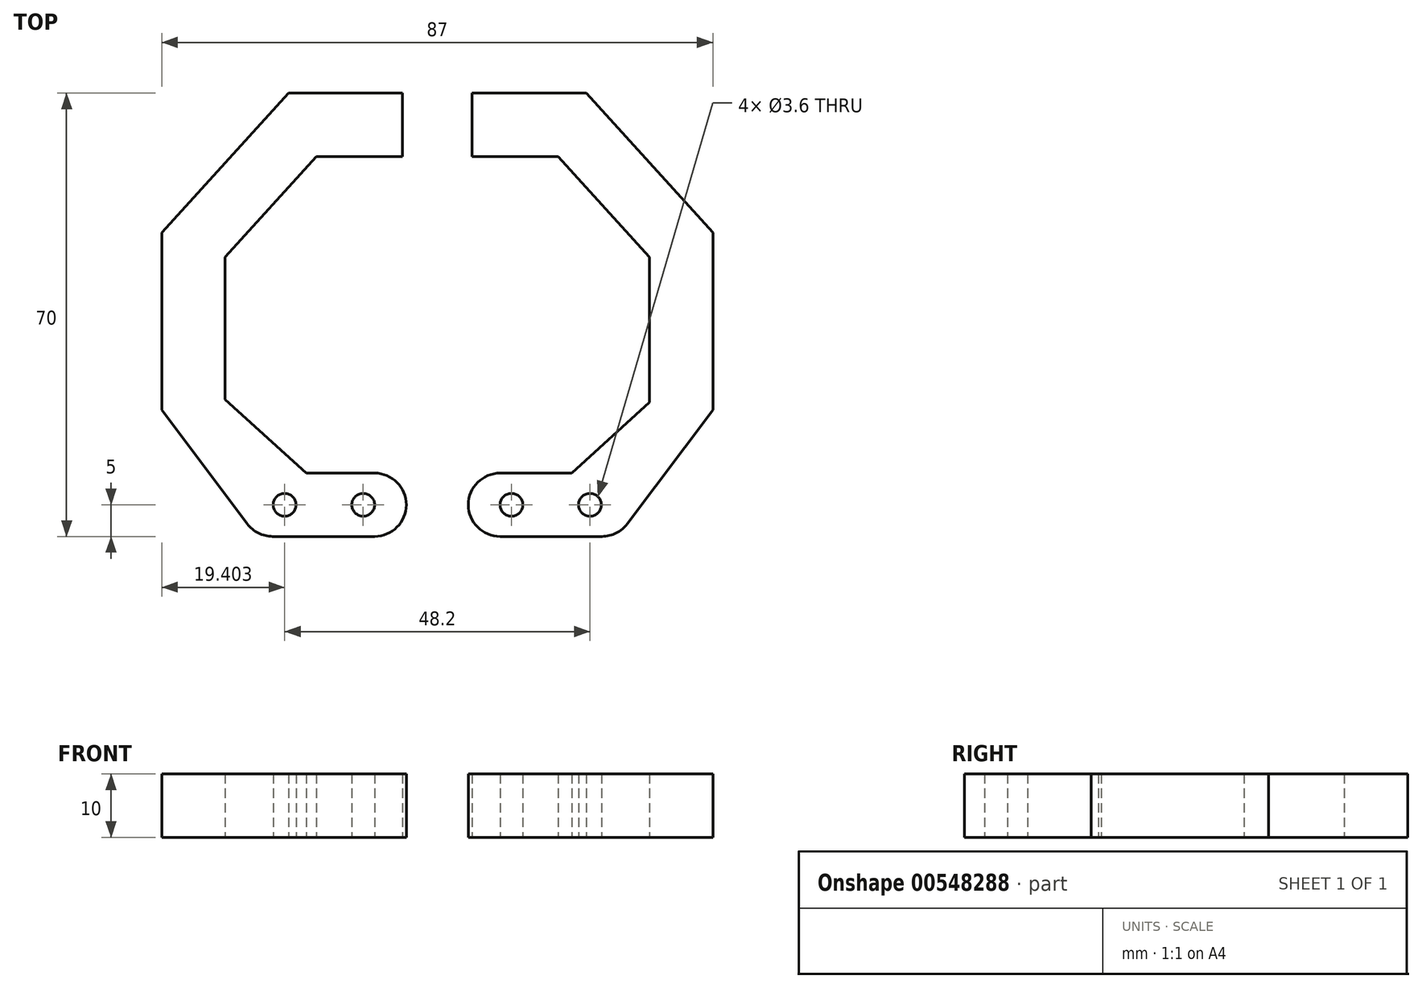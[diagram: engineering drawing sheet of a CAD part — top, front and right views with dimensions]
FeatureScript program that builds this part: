
annotation { "Feature Type Name" : "Feature", "Feature Type Description" : "" }
export const myFeature = defineFeature(function(context is Context, id is Id, definition is map)
    precondition{}
    {
        {
            var Q0;
            Q0=qCreatedBy(makeId("Top.planeOp"),FACE);
            var sketch = newSketch(context, id + "F0", { "sketchPlane" : qUnion([Q0])});
            skLineSegment(sketch, "E0.bottom", {"start": v(28.48, -32.9) * mm, "end": v(4.88, -32.9) * mm});
            skLineSegment(sketch, "E0.top", {"start": v(23.48, 37.1) * mm, "end": v(5.48, 37.1) * mm});
            skLineSegment(sketch, "E0.left", {"start": v(43.48, -12.9) * mm, "end": v(43.48, 15.1) * mm});
            skLineSegment(sketch, "E0.right", {"start": v(-43.52, -12.9) * mm, "end": v(-43.52, 15.1) * mm});
            skPoint(sketch, "E0.middle", {"position": v(-0.02, 2.1) * mm});
            skLineSegment(sketch, "E1", {"start": v(-43.52, -12.9) * mm, "end": v(-28.52, -32.9) * mm});
            skLineSegment(sketch, "E2", {"start": v(28.48, -32.9) * mm, "end": v(43.48, -12.9) * mm});
            skLineSegment(sketch, "E3", {"start": v(-43.52, 15.1) * mm, "end": v(-23.52, 37.1) * mm});
            skLineSegment(sketch, "E4", {"start": v(43.48, 15.1) * mm, "end": v(23.48, 37.1) * mm});
            skLineSegment(sketch, "E5", {"start": v(-23.52, 37.1) * mm, "end": v(-5.52, 37.1) * mm});
            skLineSegment(sketch, "E6", {"start": v(-5.52, 37.1) * mm, "end": v(-5.52, 27.1) * mm});
            skLineSegment(sketch, "E7", {"start": v(-5.52, 27.1) * mm, "end": v(-19.1, 27.1) * mm});
            skLineSegment(sketch, "E8", {"start": v(-19.1, 27.1) * mm, "end": v(-33.52, 11.23) * mm});
            skLineSegment(sketch, "E9", {"start": v(-33.52, 11.23) * mm, "end": v(-33.52, -11.26) * mm});
            skLineSegment(sketch, "E10", {"start": v(-33.52, -11.26) * mm, "end": v(-20.71, -22.9) * mm});
            skLineSegment(sketch, "E11", {"start": v(-20.71, -22.9) * mm, "end": v(-4.92, -22.9) * mm});
            skLineSegment(sketch, "E12", {"start": v(-4.92, -22.9) * mm, "end": v(-4.92, -32.9) * mm});
            skLineSegment(sketch, "E13", {"start": v(5.48, 37.1) * mm, "end": v(5.48, 27.1) * mm});
            skLineSegment(sketch, "E14", {"start": v(5.48, 27.1) * mm, "end": v(19.06, 27.1) * mm});
            skLineSegment(sketch, "E15", {"start": v(19.06, 27.1) * mm, "end": v(33.48, 11.23) * mm});
            skLineSegment(sketch, "E16", {"start": v(33.48, 11.23) * mm, "end": v(33.48, -11.72) * mm});
            skLineSegment(sketch, "E17", {"start": v(33.48, -11.72) * mm, "end": v(21.18, -22.9) * mm});
            skLineSegment(sketch, "E18", {"start": v(21.18, -22.9) * mm, "end": v(4.88, -22.9) * mm});
            skLineSegment(sketch, "E19", {"start": v(4.88, -22.9) * mm, "end": v(4.88, -32.9) * mm});
            skCircle(sketch, "E20", {"center": v(11.68, -27.9) * mm, "radius": 1.8 * mm});
            skCircle(sketch, "E21", {"center": v(-11.72, -27.9) * mm, "radius": 1.8 * mm});
            skCircle(sketch, "E22", {"center": v(24.08, -27.9) * mm, "radius": 1.8 * mm});
            skCircle(sketch, "E23", {"center": v(-24.12, -27.9) * mm, "radius": 1.8 * mm});
            skPoint(sketch, "E24.orphan", {"position": v(-43.52, 37.1) * mm});
            skLineSegment(sketch, "E25.trimOffspring", {"start": v(-5.52, 37.1) * mm, "end": v(-23.52, 37.1) * mm});
            skPoint(sketch, "E26.orphan", {"position": v(43.48, 37.1) * mm});
            skPoint(sketch, "E27.orphan", {"position": v(43.48, -32.9) * mm});
            skLineSegment(sketch, "E28.trimOffspring", {"start": v(-4.92, -32.9) * mm, "end": v(-28.52, -32.9) * mm});
            skPoint(sketch, "E29.orphan", {"position": v(-43.52, -32.9) * mm});
            skSolve(sketch);
        }
        {
            var Q0;
            Q0=qSketchRegion(id+"F0",true);
            extrude(context, id + "F1", {"entities" : qUnion([Q0]), "depth" : 10 * mm, "offsetDistance" : 25 * mm});
        }
        {
            var Q0;
            Q0=makeQuery(id+"F1.opExtrude","SWEPT_EDGE",EDGE,{"disambiguationData":[OSD([sQuery(id+"F0.wireOp",EDGE,"E12"),sQuery(id+"F0.wireOp",EDGE,"E28.trimOffspring")])]});
            var Q1;
            Q1=makeQuery(id+"F1.opExtrude","SWEPT_EDGE",EDGE,{"disambiguationData":[OSD([sQuery(id+"F0.wireOp",EDGE,"E11"),sQuery(id+"F0.wireOp",EDGE,"E12")])]});
            var Q2;
            Q2=makeQuery(id+"F1.opExtrude","SWEPT_EDGE",EDGE,{"disambiguationData":[OSD([sQuery(id+"F0.wireOp",EDGE,"E18"),sQuery(id+"F0.wireOp",EDGE,"E19")])]});
            var Q3;
            Q3=makeQuery(id+"F1.opExtrude","SWEPT_EDGE",EDGE,{"disambiguationData":[OSD([sQuery(id+"F0.wireOp",EDGE,"E0.bottom"),sQuery(id+"F0.wireOp",EDGE,"E19")])]});
            fillet(context, id + "F2", {"entities" : qUnion([Q0, Q1, Q2, Q3]), "radius" : 5 * mm, "tangentPropagation" : true, "allowEdgeOverflow" : false});
        }
        {
            var Q0;
            Q0=makeQuery(id+"F1.opExtrude","SWEPT_EDGE",EDGE,{"disambiguationData":[OSD([sQuery(id+"F0.wireOp",EDGE,"E1"),sQuery(id+"F0.wireOp",EDGE,"E28.trimOffspring")])]});
            var Q1;
            Q1=makeQuery(id+"F1.opExtrude","SWEPT_EDGE",EDGE,{"disambiguationData":[OSD([sQuery(id+"F0.wireOp",EDGE,"E0.bottom"),sQuery(id+"F0.wireOp",EDGE,"E2")])]});
            fillet(context, id + "F3", {"entities" : qUnion([Q0, Q1]), "radius" : 5 * mm, "tangentPropagation" : true, "allowEdgeOverflow" : false});
        }
    });
